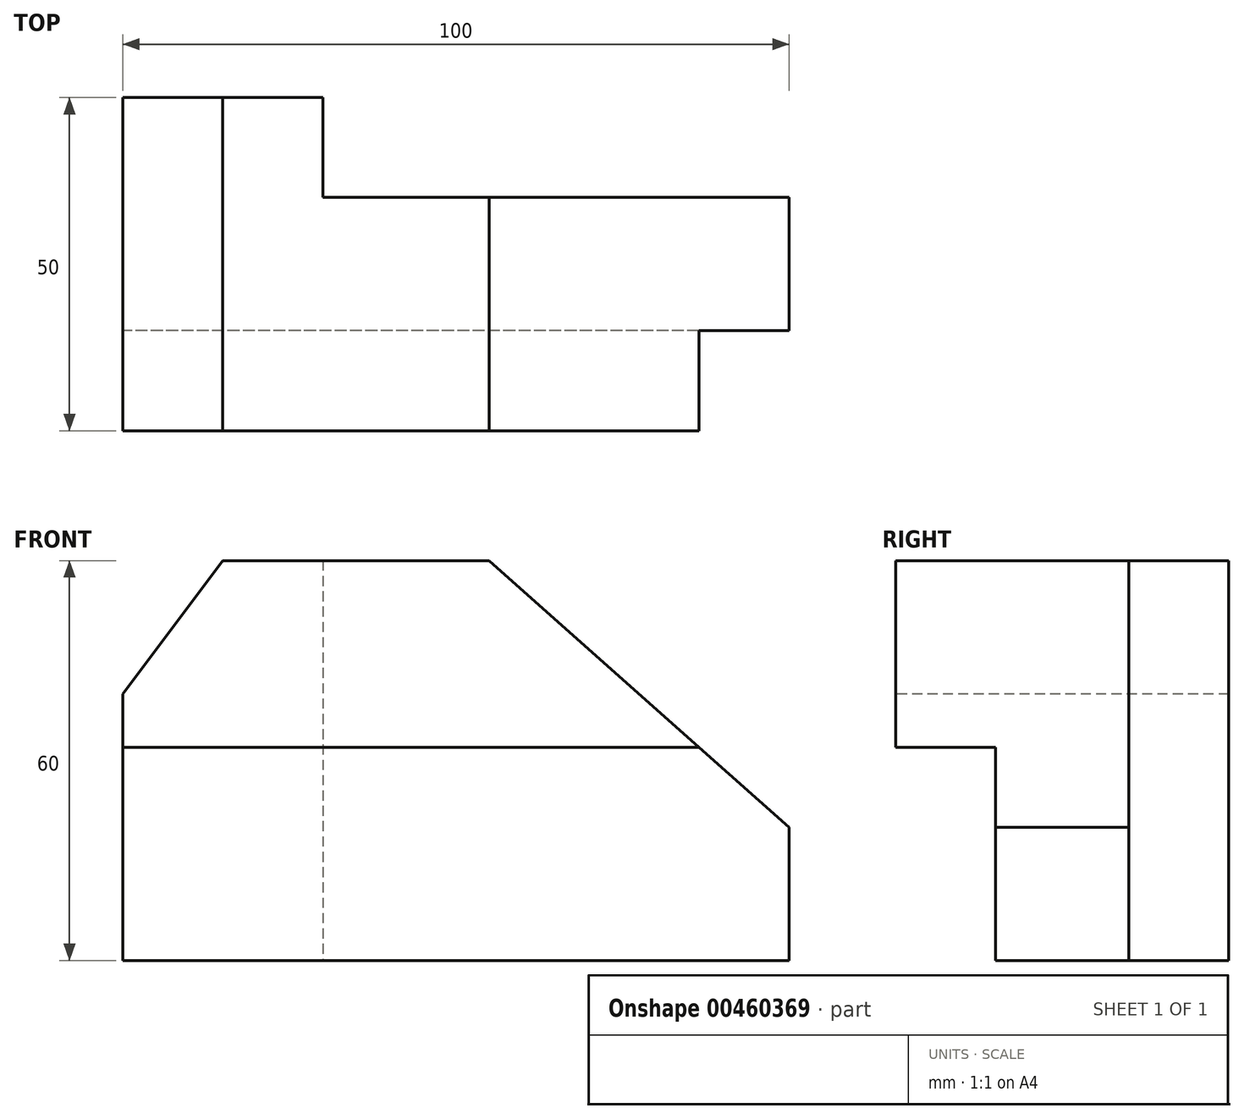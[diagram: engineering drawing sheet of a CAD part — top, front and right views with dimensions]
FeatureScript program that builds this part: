
annotation { "Feature Type Name" : "Feature", "Feature Type Description" : "" }
export const myFeature = defineFeature(function(context is Context, id is Id, definition is map)
    precondition{}
    {
        {
            var Q0;
            Q0=qCreatedBy(makeId("Top.planeOp"),FACE);
            var sketch = newSketch(context, id + "F0", { "sketchPlane" : qUnion([Q0])});
            skLineSegment(sketch, "E0.bottom", {"start": v(0, 0) * mm, "end": v(100, 0) * mm});
            skLineSegment(sketch, "E0.top", {"start": v(0, 50) * mm, "end": v(100, 50) * mm});
            skLineSegment(sketch, "E0.left", {"start": v(0, 0) * mm, "end": v(0, 50) * mm});
            skLineSegment(sketch, "E0.right", {"start": v(100, 0) * mm, "end": v(100, 50) * mm});
            skSolve(sketch);
        }
        {
            var Q0;
            Q0=makeQuery(id+"F0.imprint","IMPRINT",FACE,{"disambiguationData":[TD([[makeQuery(id+"F0.imprint","IMPRINT",EDGE,{"derivedFrom":sQuery(id+"F0.wireOp",EDGE,"E0.bottom")}),1.0]])]});
            extrude(context, id + "F1", {"entities" : qUnion([Q0]), "depth" : 60 * mm});
        }
        {
            var Q0;
            Q0=makeQuery(id+"F1.opExtrude","SWEPT_FACE",FACE,{"disambiguationData":[OSD([sQuery(id+"F0.wireOp",EDGE,"E0.bottom")])]});
            var sketch = newSketch(context, id + "F2", { "sketchPlane" : qUnion([Q0])});
            skLineSegment(sketch, "E1", {"start": v(15, 60) * mm, "end": v(0, 40) * mm});
            skLineSegment(sketch, "E2", {"start": v(55, 60) * mm, "end": v(100, 20) * mm});
            skSolve(sketch);
        }
        {
            var Q0;
            {var subQ0=sQuery(id+"F2.wireOp",EDGE,"E1");Q0=makeQuery(id+"F2.imprint","IMPRINT",FACE,{"disambiguationData":[TD([[makeQuery(id+"F2.imprint","IMPRINT",EDGE,{"derivedFrom":subQ0}),-1.0]])]});}
            extrude(context, id + "F3", {"entities" : qUnion([Q0]), "operationType" : NewBodyOperationType.REMOVE, "endBound" : BoundingType.UP_TO_NEXT, "oppositeDirection" : true, "depth" : 25 * mm});
        }
        {
            var Q0;
            Q0=makeQuery(id+"F1.opExtrude","SWEPT_FACE",FACE,{"disambiguationData":[OSD([sQuery(id+"F0.wireOp",EDGE,"E0.bottom")])]});
            var sketch = newSketch(context, id + "F4", { "sketchPlane" : qUnion([Q0])});
            skLineSegment(sketch, "E3", {"start": v(55, 60) * mm, "end": v(100, 20) * mm});
            skLineSegment(sketch, "E4", {"start": v(100, 20) * mm, "end": v(100, 60) * mm});
            skLineSegment(sketch, "E5", {"start": v(100, 60) * mm, "end": v(55, 60) * mm});
            skSolve(sketch);
        }
        {
            var Q0;
            Q0=makeQuery(id+"F4.imprint","IMPRINT",FACE,{"disambiguationData":[TD([[makeQuery(id+"F4.imprint","IMPRINT",EDGE,{"derivedFrom":sQuery(id+"F4.wireOp",EDGE,"E3")}),1.0]])]});
            extrude(context, id + "F5", {"entities" : qUnion([Q0]), "operationType" : NewBodyOperationType.REMOVE, "endBound" : BoundingType.UP_TO_NEXT, "oppositeDirection" : true, "depth" : 25 * mm});
        }
        {
            var Q0;
            Q0=makeQuery(id+"F1.opExtrude","SWEPT_FACE",FACE,{"disambiguationData":[OSD([sQuery(id+"F0.wireOp",EDGE,"E0.left")])]});
            var sketch = newSketch(context, id + "F6", { "sketchPlane" : qUnion([Q0])});
            skLineSegment(sketch, "E6", {"start": v(0, 32) * mm, "end": v(-15, 32) * mm});
            skLineSegment(sketch, "E7", {"start": v(-15, 32) * mm, "end": v(-15, 0) * mm});
            skLineSegment(sketch, "E8", {"start": v(-15, 0) * mm, "end": v(0, 0) * mm});
            skLineSegment(sketch, "E9", {"start": v(0, 0) * mm, "end": v(0, 32) * mm});
            skSolve(sketch);
        }
        {
            var Q0;
            Q0 = qSketchRegion(id + "F6", true);
            extrude(context, id + "F7", {"entities" : qUnion([Q0]), "operationType" : NewBodyOperationType.REMOVE, "endBound" : BoundingType.UP_TO_NEXT, "oppositeDirection" : true, "depth" : 25 * mm});
        }
        {
            var Q0;
            Q0=makeQuery(id+"F1.opExtrude","CAP_FACE",FACE,{"disambiguationData":[OSD([sQuery(id+"F0.wireOp",EDGE,"E0.bottom"),sQuery(id+"F0.wireOp",EDGE,"E0.top"),sQuery(id+"F0.wireOp",EDGE,"E0.left"),sQuery(id+"F0.wireOp",EDGE,"E0.right")])],"isStart":true});
            var sketch = newSketch(context, id + "F8", { "sketchPlane" : qUnion([Q0])});
            skLineSegment(sketch, "E10", {"start": v(100, -50) * mm, "end": v(30, -50) * mm});
            skLineSegment(sketch, "E11", {"start": v(30, -50) * mm, "end": v(30, -35) * mm});
            skLineSegment(sketch, "E12", {"start": v(30, -35) * mm, "end": v(100, -35) * mm});
            skLineSegment(sketch, "E13", {"start": v(100, -35) * mm, "end": v(100, -50) * mm});
            skSolve(sketch);
        }
        {
            var Q0;
            Q0 = qSketchRegion(id + "F8", true);
            extrude(context, id + "F9", {"entities" : qUnion([Q0]), "operationType" : NewBodyOperationType.REMOVE, "endBound" : BoundingType.UP_TO_NEXT, "oppositeDirection" : true, "depth" : 25 * mm});
        }
    });
